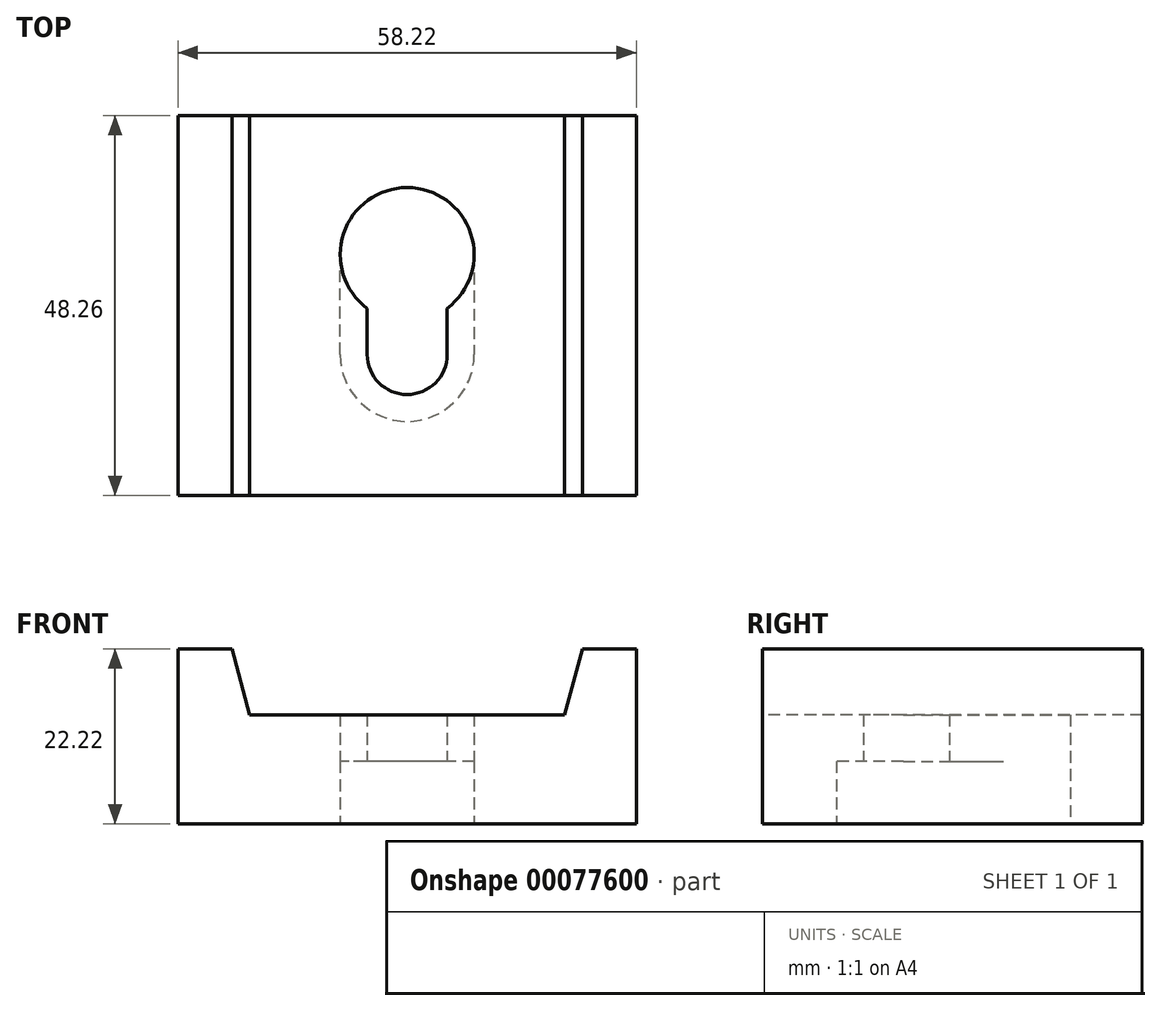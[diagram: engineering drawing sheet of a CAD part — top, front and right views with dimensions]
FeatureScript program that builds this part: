
annotation { "Feature Type Name" : "Feature", "Feature Type Description" : "" }
export const myFeature = defineFeature(function(context is Context, id is Id, definition is map)
    precondition{}
    {
        {
            var Q0;
            Q0=qCreatedBy(makeId("Front.planeOp"),FACE);
            var sketch = newSketch(context, id + "F0", { "sketchPlane" : qUnion([Q0])});
            skLineSegment(sketch, "E0.bottom", {"start": v(29.1, 11.11) * mm, "end": v(-29.1, 11.11) * mm});
            skLineSegment(sketch, "E0.top", {"start": v(29.1, -11.11) * mm, "end": v(-29.1, -11.11) * mm});
            skLineSegment(sketch, "E0.left", {"start": v(29.1, 11.11) * mm, "end": v(29.1, -11.11) * mm});
            skLineSegment(sketch, "E0.right", {"start": v(-29.1, 11.11) * mm, "end": v(-29.1, -11.11) * mm});
            skPoint(sketch, "E0.middle", {"position": v(0, 0) * mm});
            skSolve(sketch);
        }
        {
            var Q0;
            Q0 = qSketchRegion(id + "F0", true);
            extrude(context, id + "F1", {"entities" : qUnion([Q0]), "depth" : 48.26 * mm});
        }
        {
            var Q0;
            Q0=makeQuery(id+"F1.opExtrude","CAP_FACE",FACE,{"disambiguationData":[OSD([sQuery(id+"F0.wireOp",EDGE,"E0.bottom"),sQuery(id+"F0.wireOp",EDGE,"E0.top"),sQuery(id+"F0.wireOp",EDGE,"E0.left"),sQuery(id+"F0.wireOp",EDGE,"E0.right")])],"isStart":false});
            var sketch = newSketch(context, id + "F2", { "sketchPlane" : qUnion([Q0])});
            skLineSegment(sketch, "E1.top", {"start": v(-20.01, 2.76) * mm, "end": v(20.01, 2.76) * mm});
            skLineSegment(sketch, "E2", {"start": v(-29.1, 11.11) * mm, "end": v(-22.25, 11.11) * mm});
            skLineSegment(sketch, "E3", {"start": v(-22.25, 11.11) * mm, "end": v(-20.01, 2.76) * mm});
            skLineSegment(sketch, "E4", {"start": v(29.1, 11.11) * mm, "end": v(22.25, 11.11) * mm});
            skLineSegment(sketch, "E5", {"start": v(22.25, 11.11) * mm, "end": v(20.01, 2.76) * mm});
            skLineSegment(sketch, "E6", {"start": v(-29.1, 11.11) * mm, "end": v(-29.1, 14.91) * mm});
            skLineSegment(sketch, "E7", {"start": v(-29.1, 14.91) * mm, "end": v(29.1, 14.91) * mm});
            skLineSegment(sketch, "E8", {"start": v(29.1, 14.91) * mm, "end": v(29.1, 11.11) * mm});
            skSolve(sketch);
        }
        {
            var Q0;
            Q0 = qSketchRegion(id + "F2", true);
            extrude(context, id + "F3", {"entities" : qUnion([Q0]), "operationType" : NewBodyOperationType.REMOVE, "endBound" : BoundingType.THROUGH_ALL, "oppositeDirection" : true, "depth" : 25.4 * mm});
        }
        {
            var Q0;
            Q0=makeQuery(id+"F1.opExtrude","SWEPT_FACE",FACE,{"disambiguationData":[OSD([sQuery(id+"F0.wireOp",EDGE,"E0.top")])]});
            var sketch = newSketch(context, id + "F4", { "sketchPlane" : qUnion([Q0])});
            skArc(sketch, "E9", {"start": v(8.5, 30.35) * mm, "mid": v(0, 38.86) * mm, "end": v(-8.5, 30.35) * mm});
            skArc(sketch, "E10", {"start": v(-8.5, 17.65) * mm, "mid": v(0, 9.14) * mm, "end": v(8.5, 17.65) * mm});
            skLineSegment(sketch, "E11", {"start": v(-8.5, 30.35) * mm, "end": v(-8.5, 17.65) * mm});
            skLineSegment(sketch, "E12", {"start": v(8.5, 17.65) * mm, "end": v(8.5, 30.35) * mm});
            skSolve(sketch);
        }
        {
            var Q0;
            Q0 = qSketchRegion(id + "F4", true);
            extrude(context, id + "F5", {"entities" : qUnion([Q0]), "operationType" : NewBodyOperationType.REMOVE, "oppositeDirection" : true, "depth" : 7.95 * mm});
        }
        {
            var Q0;
            Q0=makeQuery(id+"F5.boolean.opBoolean","COPY",FACE,{"derivedFrom":makeQuery(id+"F5.opExtrude","CAP_FACE",FACE,{"disambiguationData":[OSD([sQuery(id+"F4.wireOp",EDGE,"E9"),sQuery(id+"F4.wireOp",EDGE,"E10"),sQuery(id+"F4.wireOp",EDGE,"E11"),sQuery(id+"F4.wireOp",EDGE,"E12")])],"isStart":false})});
            var sketch = newSketch(context, id + "F6", { "sketchPlane" : qUnion([Q0])});
            skArc(sketch, "E13", {"start": v(-5.08, 24.48) * mm, "mid": v(0, 9.14) * mm, "end": v(5.08, 24.48) * mm});
            skArc(sketch, "E14", {"start": v(5.08, 30.35) * mm, "mid": v(0, 35.43) * mm, "end": v(-5.08, 30.35) * mm});
            skLineSegment(sketch, "E15", {"start": v(-5.08, 30.35) * mm, "end": v(-5.08, 24.48) * mm});
            skLineSegment(sketch, "E16", {"start": v(5.08, 30.35) * mm, "end": v(5.08, 24.48) * mm});
            skSolve(sketch);
        }
        {
            var Q0;
            Q0 = qSketchRegion(id + "F6", true);
            extrude(context, id + "F7", {"entities" : qUnion([Q0]), "operationType" : NewBodyOperationType.REMOVE, "endBound" : BoundingType.THROUGH_ALL, "oppositeDirection" : true, "depth" : 25.4 * mm});
        }
    });
